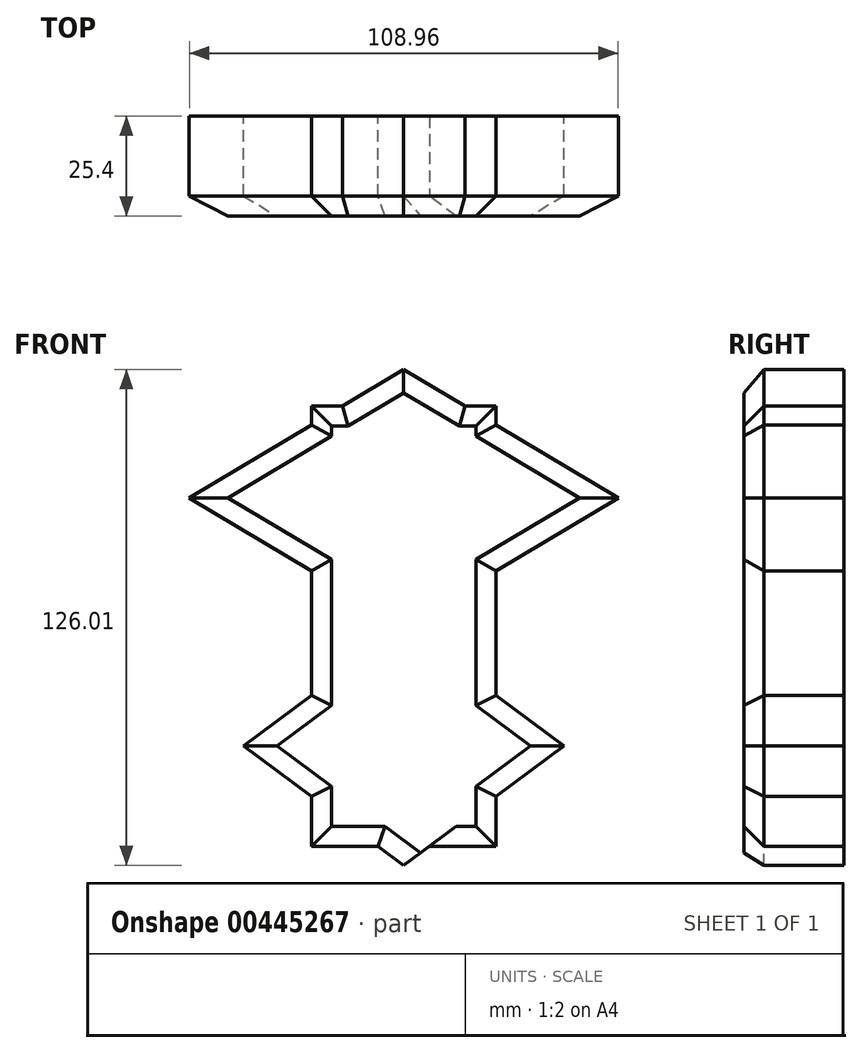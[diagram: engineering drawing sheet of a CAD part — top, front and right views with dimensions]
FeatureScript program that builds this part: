
annotation { "Feature Type Name" : "Feature", "Feature Type Description" : "" }
export const myFeature = defineFeature(function(context is Context, id is Id, definition is map)
    precondition{}
    {
        {
            var Q0;
            Q0=qCreatedBy(makeId("Front.planeOp"),FACE);
            var sketch = newSketch(context, id + "F0", { "sketchPlane" : qUnion([Q0])});
            skLineSegment(sketch, "E0.bottom", {"start": v(23.47, 55.93) * mm, "end": v(-23.47, 55.93) * mm});
            skLineSegment(sketch, "E0.top", {"start": v(23.47, -55.93) * mm, "end": v(-23.47, -55.93) * mm});
            skLineSegment(sketch, "E0.left", {"start": v(23.47, 55.93) * mm, "end": v(23.47, -55.93) * mm});
            skLineSegment(sketch, "E0.right", {"start": v(-23.47, 55.93) * mm, "end": v(-23.47, -55.93) * mm});
            skPoint(sketch, "E0.middle", {"position": v(0, 0) * mm});
            skSolve(sketch);
        }
        {
            var Q0;
            Q0=makeQuery(id+"F0.imprint","IMPRINT",FACE,{"disambiguationData":[TD([[makeQuery(id+"F0.imprint","IMPRINT",EDGE,{"derivedFrom":sQuery(id+"F0.wireOp",EDGE,"E0.bottom")}),1.0]])]});
            var sketch = newSketch(context, id + "F1", { "sketchPlane" : qUnion([Q0])});
            skLineSegment(sketch, "E1", {"start": v(0, 0) * mm, "end": v(54.48, 32.61) * mm});
            skLineSegment(sketch, "E2", {"start": v(54.48, 32.61) * mm, "end": v(0, 65.23) * mm});
            skLineSegment(sketch, "E3", {"start": v(0, 65.23) * mm, "end": v(-54.48, 32.61) * mm});
            skLineSegment(sketch, "E4", {"start": v(-54.48, 32.61) * mm, "end": v(0, 0) * mm});
            skSolve(sketch);
        }
        {
            var Q0;
            Q0=qCreatedBy(makeId("Front.planeOp"),FACE);
            var sketch = newSketch(context, id + "F2", { "sketchPlane" : qUnion([Q0])});
            skLineSegment(sketch, "E5", {"start": v(0, -60.78) * mm, "end": v(-40.7, -30.4) * mm});
            skLineSegment(sketch, "E6", {"start": v(-40.7, -30.4) * mm, "end": v(0, 0) * mm});
            skLineSegment(sketch, "E7", {"start": v(0, 0) * mm, "end": v(40.7, -30.4) * mm});
            skLineSegment(sketch, "E8", {"start": v(40.7, -30.4) * mm, "end": v(0, -60.78) * mm});
            skSolve(sketch);
        }
        {
            var Q0;
            Q0 = qSketchRegion(id + "F0", true);
            extrude(context, id + "F3", {"entities" : qUnion([Q0]), "depth" : 25.4 * mm});
        }
        {
            var Q0;
            Q0 = qSketchRegion(id + "F1", true);
            extrude(context, id + "F4", {"entities" : qUnion([Q0]), "operationType" : NewBodyOperationType.ADD, "depth" : 25.4 * mm});
        }
        {
            var Q0;
            Q0 = qSketchRegion(id + "F2", true);
            extrude(context, id + "F5", {"entities" : qUnion([Q0]), "operationType" : NewBodyOperationType.ADD, "depth" : 25.4 * mm});
        }
        {
            var Q0;
            Q0=makeQuery(id+"F4.opExtrude","CAP_EDGE",EDGE,{"disambiguationData":[OSD([sQuery(id+"F1.wireOp",EDGE,"E4")])],"isStart":false});
            var Q1;
            {var subQ0=sQuery(id+"F1.wireOp",EDGE,"E4");var subQ1=makeQuery(id+"F4.opExtrude","SWEPT_FACE",FACE,{"disambiguationData":[OSD([subQ0])]});var subQ3=sQuery(id+"F0.wireOp",EDGE,"E0.right");var subQ5=sQuery(id+"F0.wireOp",EDGE,"E0.top");Q1=makeQuery(id+"F5.boolean.opBoolean","SPLIT",EDGE,{"disambiguationData":[TD([subQ1])],"derivedFrom":makeQuery(id+"F4.boolean.opBoolean","SPLIT",EDGE,{"disambiguationData":[TD([makeQuery(id+"F3.opExtrude","SWEPT_FACE",FACE,{"disambiguationData":[OSD([subQ5])]})])],"derivedFrom":makeQuery(id+"F3.opExtrude","CAP_EDGE",EDGE,{"disambiguationData":[OSD([subQ3])],"isStart":false})})});}
            var Q2;
            Q2=makeQuery(id+"F5.opExtrude","CAP_EDGE",EDGE,{"disambiguationData":[OSD([sQuery(id+"F2.wireOp",EDGE,"E6")])],"isStart":false});
            var Q3;
            {var subQ0=sQuery(id+"F2.wireOp",EDGE,"E5");var subQ1=sQuery(id+"F0.wireOp",EDGE,"E0.right");Q3=makeQuery(id+"F5.boolean.opBoolean","SPLIT",EDGE,{"disambiguationData":[TD([makeQuery(id+"F3.opExtrude","SWEPT_FACE",FACE,{"disambiguationData":[OSD([subQ1])]})])],"derivedFrom":makeQuery(id+"F5.opExtrude","CAP_EDGE",EDGE,{"disambiguationData":[OSD([subQ0])],"isStart":false})});}
            var Q4;
            {var subQ0=sQuery(id+"F0.wireOp",EDGE,"E0.right");var subQ4=sQuery(id+"F0.wireOp",EDGE,"E0.top");var subQ5=makeQuery(id+"F3.opExtrude","SWEPT_FACE",FACE,{"disambiguationData":[OSD([subQ4])]});Q4=makeQuery(id+"F5.boolean.opBoolean","SPLIT",EDGE,{"disambiguationData":[TD([subQ5])],"derivedFrom":makeQuery(id+"F4.boolean.opBoolean","SPLIT",EDGE,{"disambiguationData":[TD([subQ5])],"derivedFrom":makeQuery(id+"F3.opExtrude","CAP_EDGE",EDGE,{"disambiguationData":[OSD([subQ0])],"isStart":false})})});}
            var Q5;
            {var subQ0=sQuery(id+"F0.wireOp",EDGE,"E0.right");var subQ1=sQuery(id+"F0.wireOp",EDGE,"E0.top");Q5=makeQuery(id+"F5.boolean.opBoolean","SPLIT",EDGE,{"disambiguationData":[TD([makeQuery(id+"F3.opExtrude","SWEPT_FACE",FACE,{"disambiguationData":[OSD([subQ0])]})])],"derivedFrom":makeQuery(id+"F3.opExtrude","CAP_EDGE",EDGE,{"disambiguationData":[OSD([subQ1])],"isStart":false})});}
            var Q6;
            {var subQ0=sQuery(id+"F2.wireOp",EDGE,"E5");var subQ2=sQuery(id+"F0.wireOp",EDGE,"E0.top");Q6=makeQuery(id+"F5.boolean.opBoolean","SPLIT",EDGE,{"disambiguationData":[TD([makeQuery(id+"F3.opExtrude","SWEPT_FACE",FACE,{"disambiguationData":[OSD([subQ2])]})])],"derivedFrom":makeQuery(id+"F5.opExtrude","CAP_EDGE",EDGE,{"disambiguationData":[OSD([subQ0])],"isStart":false})});}
            var Q7;
            {var subQ0=sQuery(id+"F0.wireOp",EDGE,"E0.left");var subQ2=sQuery(id+"F0.wireOp",EDGE,"E0.top");Q7=makeQuery(id+"F5.boolean.opBoolean","SPLIT",EDGE,{"disambiguationData":[TD([makeQuery(id+"F3.opExtrude","SWEPT_FACE",FACE,{"disambiguationData":[OSD([subQ0])]})])],"derivedFrom":makeQuery(id+"F3.opExtrude","CAP_EDGE",EDGE,{"disambiguationData":[OSD([subQ2])],"isStart":false})});}
            var Q8;
            {var subQ0=sQuery(id+"F0.wireOp",EDGE,"E0.left");var subQ5=sQuery(id+"F0.wireOp",EDGE,"E0.top");var subQ6=makeQuery(id+"F3.opExtrude","SWEPT_FACE",FACE,{"disambiguationData":[OSD([subQ5])]});Q8=makeQuery(id+"F5.boolean.opBoolean","SPLIT",EDGE,{"disambiguationData":[TD([subQ6])],"derivedFrom":makeQuery(id+"F4.boolean.opBoolean","SPLIT",EDGE,{"disambiguationData":[TD([subQ6])],"derivedFrom":makeQuery(id+"F3.opExtrude","CAP_EDGE",EDGE,{"disambiguationData":[OSD([subQ0])],"isStart":false})})});}
            var Q9;
            {var subQ0=sQuery(id+"F2.wireOp",EDGE,"E8");var subQ2=sQuery(id+"F0.wireOp",EDGE,"E0.left");Q9=makeQuery(id+"F5.boolean.opBoolean","SPLIT",EDGE,{"disambiguationData":[TD([makeQuery(id+"F3.opExtrude","SWEPT_FACE",FACE,{"disambiguationData":[OSD([subQ2])]})])],"derivedFrom":makeQuery(id+"F5.opExtrude","CAP_EDGE",EDGE,{"disambiguationData":[OSD([subQ0])],"isStart":false})});}
            var Q10;
            Q10=makeQuery(id+"F5.opExtrude","CAP_EDGE",EDGE,{"disambiguationData":[OSD([sQuery(id+"F2.wireOp",EDGE,"E7")])],"isStart":false});
            var Q11;
            {var subQ0=sQuery(id+"F1.wireOp",EDGE,"E1");var subQ2=makeQuery(id+"F4.opExtrude","SWEPT_FACE",FACE,{"disambiguationData":[OSD([subQ0])]});var subQ3=sQuery(id+"F0.wireOp",EDGE,"E0.left");var subQ5=sQuery(id+"F0.wireOp",EDGE,"E0.top");Q11=makeQuery(id+"F5.boolean.opBoolean","SPLIT",EDGE,{"disambiguationData":[TD([subQ2])],"derivedFrom":makeQuery(id+"F4.boolean.opBoolean","SPLIT",EDGE,{"disambiguationData":[TD([makeQuery(id+"F3.opExtrude","SWEPT_FACE",FACE,{"disambiguationData":[OSD([subQ5])]})])],"derivedFrom":makeQuery(id+"F3.opExtrude","CAP_EDGE",EDGE,{"disambiguationData":[OSD([subQ3])],"isStart":false})})});}
            var Q12;
            Q12=makeQuery(id+"F4.opExtrude","CAP_EDGE",EDGE,{"disambiguationData":[OSD([sQuery(id+"F1.wireOp",EDGE,"E1")])],"isStart":false});
            var Q13;
            {var subQ0=sQuery(id+"F1.wireOp",EDGE,"E2");var subQ2=sQuery(id+"F0.wireOp",EDGE,"E0.left");Q13=makeQuery(id+"F4.boolean.opBoolean","SPLIT",EDGE,{"disambiguationData":[TD([makeQuery(id+"F3.opExtrude","SWEPT_FACE",FACE,{"disambiguationData":[OSD([subQ2])]})])],"derivedFrom":makeQuery(id+"F4.opExtrude","CAP_EDGE",EDGE,{"disambiguationData":[OSD([subQ0])],"isStart":false})});}
            var Q14;
            {var subQ1=sQuery(id+"F0.wireOp",EDGE,"E0.left");var subQ2=sQuery(id+"F0.wireOp",EDGE,"E0.bottom");Q14=makeQuery(id+"F4.boolean.opBoolean","SPLIT",EDGE,{"disambiguationData":[TD([makeQuery(id+"F3.opExtrude","SWEPT_FACE",FACE,{"disambiguationData":[OSD([subQ2])]})])],"derivedFrom":makeQuery(id+"F3.opExtrude","CAP_EDGE",EDGE,{"disambiguationData":[OSD([subQ1])],"isStart":false})});}
            var Q15;
            {var subQ1=sQuery(id+"F0.wireOp",EDGE,"E0.left");var subQ2=sQuery(id+"F0.wireOp",EDGE,"E0.bottom");Q15=makeQuery(id+"F4.boolean.opBoolean","SPLIT",EDGE,{"disambiguationData":[TD([makeQuery(id+"F3.opExtrude","SWEPT_FACE",FACE,{"disambiguationData":[OSD([subQ1])]})])],"derivedFrom":makeQuery(id+"F3.opExtrude","CAP_EDGE",EDGE,{"disambiguationData":[OSD([subQ2])],"isStart":false})});}
            var Q16;
            {var subQ0=sQuery(id+"F1.wireOp",EDGE,"E2");var subQ2=sQuery(id+"F0.wireOp",EDGE,"E0.bottom");Q16=makeQuery(id+"F4.boolean.opBoolean","SPLIT",EDGE,{"disambiguationData":[TD([makeQuery(id+"F3.opExtrude","SWEPT_FACE",FACE,{"disambiguationData":[OSD([subQ2])]})])],"derivedFrom":makeQuery(id+"F4.opExtrude","CAP_EDGE",EDGE,{"disambiguationData":[OSD([subQ0])],"isStart":false})});}
            var Q17;
            {var subQ1=sQuery(id+"F1.wireOp",EDGE,"E3");var subQ2=sQuery(id+"F0.wireOp",EDGE,"E0.bottom");Q17=makeQuery(id+"F4.boolean.opBoolean","SPLIT",EDGE,{"disambiguationData":[TD([makeQuery(id+"F3.opExtrude","SWEPT_FACE",FACE,{"disambiguationData":[OSD([subQ2])]})])],"derivedFrom":makeQuery(id+"F4.opExtrude","CAP_EDGE",EDGE,{"disambiguationData":[OSD([subQ1])],"isStart":false})});}
            var Q18;
            {var subQ1=sQuery(id+"F0.wireOp",EDGE,"E0.right");var subQ2=sQuery(id+"F0.wireOp",EDGE,"E0.bottom");Q18=makeQuery(id+"F4.boolean.opBoolean","SPLIT",EDGE,{"disambiguationData":[TD([makeQuery(id+"F3.opExtrude","SWEPT_FACE",FACE,{"disambiguationData":[OSD([subQ1])]})])],"derivedFrom":makeQuery(id+"F3.opExtrude","CAP_EDGE",EDGE,{"disambiguationData":[OSD([subQ2])],"isStart":false})});}
            var Q19;
            {var subQ1=sQuery(id+"F0.wireOp",EDGE,"E0.right");var subQ2=sQuery(id+"F0.wireOp",EDGE,"E0.bottom");Q19=makeQuery(id+"F4.boolean.opBoolean","SPLIT",EDGE,{"disambiguationData":[TD([makeQuery(id+"F3.opExtrude","SWEPT_FACE",FACE,{"disambiguationData":[OSD([subQ2])]})])],"derivedFrom":makeQuery(id+"F3.opExtrude","CAP_EDGE",EDGE,{"disambiguationData":[OSD([subQ1])],"isStart":false})});}
            var Q20;
            {var subQ1=sQuery(id+"F1.wireOp",EDGE,"E3");var subQ2=sQuery(id+"F0.wireOp",EDGE,"E0.right");Q20=makeQuery(id+"F4.boolean.opBoolean","SPLIT",EDGE,{"disambiguationData":[TD([makeQuery(id+"F3.opExtrude","SWEPT_FACE",FACE,{"disambiguationData":[OSD([subQ2])]})])],"derivedFrom":makeQuery(id+"F4.opExtrude","CAP_EDGE",EDGE,{"disambiguationData":[OSD([subQ1])],"isStart":false})});}
            chamfer(context, id + "F6", {"entities" : qUnion([Q0, Q1, Q2, Q3, Q4, Q5, Q6, Q7, Q8, Q9, Q10, Q11, Q12, Q13, Q14, Q15, Q16, Q17, Q18, Q19, Q20]), "width" : 5.08 * mm, "tangentPropagation" : true});
        }
    });
